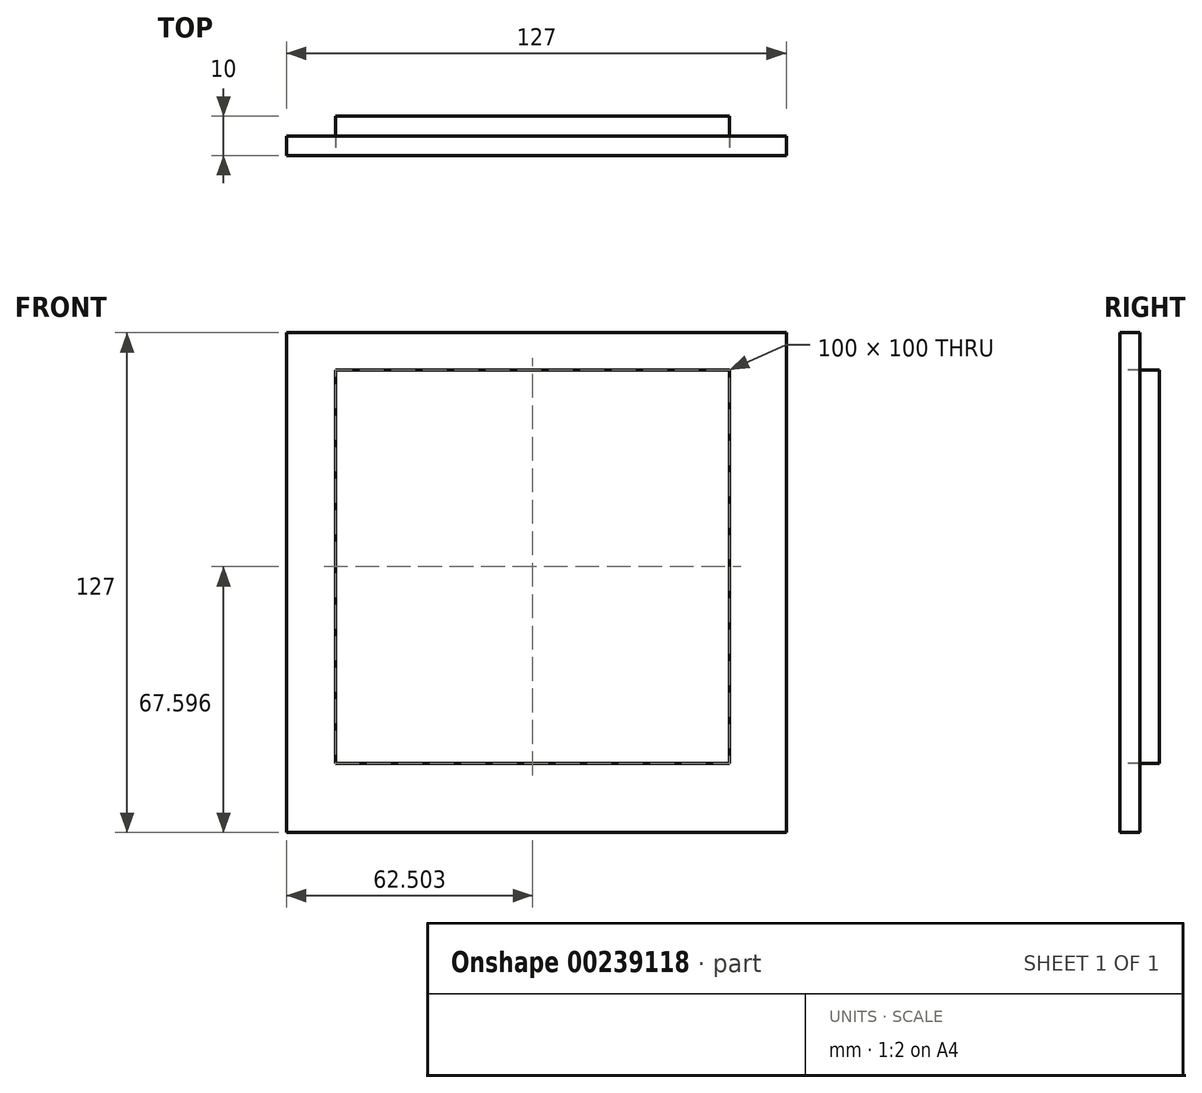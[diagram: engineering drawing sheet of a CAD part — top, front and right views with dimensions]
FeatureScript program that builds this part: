
annotation { "Feature Type Name" : "Feature", "Feature Type Description" : "" }
export const myFeature = defineFeature(function(context is Context, id is Id, definition is map)
    precondition{}
    {
        {
            assignVariable(context, id + "F0", {"name" : "L", "anyValue" : 5});
        }
        {
            var Q0;
            Q0=qCreatedBy(makeId("Front.planeOp"),FACE);
            var sketch = newSketch(context, id + "F1", { "sketchPlane" : qUnion([Q0])});
            skLineSegment(sketch, "E0.bottom", {"start": v(63.5, 63.5) * mm, "end": v(-63.5, 63.5) * mm});
            skLineSegment(sketch, "E0.top", {"start": v(63.5, -63.5) * mm, "end": v(-63.5, -63.5) * mm});
            skLineSegment(sketch, "E0.left", {"start": v(63.5, 63.5) * mm, "end": v(63.5, -63.5) * mm});
            skLineSegment(sketch, "E0.right", {"start": v(-63.5, 63.5) * mm, "end": v(-63.5, -63.5) * mm});
            skPoint(sketch, "E0.middle", {"position": v(0, 0) * mm});
            skSolve(sketch);
        }
        {
            var Q0;
            Q0 = qSketchRegion(id + "F1", true);
            extrude(context, id + "F2", {"entities" : qUnion([Q0]), "endBound" : BoundingType.SYMMETRIC, "depth" : (getVariable(context, 'L')) * mm});
        }
        {
            var Q0;
            Q0=makeQuery(id+"F2.opExtrude","CAP_FACE",FACE,{"disambiguationData":[OSD([sQuery(id+"F1.wireOp",EDGE,"E0.bottom"),sQuery(id+"F1.wireOp",EDGE,"E0.top"),sQuery(id+"F1.wireOp",EDGE,"E0.left"),sQuery(id+"F1.wireOp",EDGE,"E0.right")])],"isStart":false});
            var sketch = newSketch(context, id + "F3", { "sketchPlane" : qUnion([Q0])});
            skLineSegment(sketch, "E1.bottom", {"start": v(49, -45.9) * mm, "end": v(-51, -45.9) * mm});
            skLineSegment(sketch, "E1.top", {"start": v(49, 54.1) * mm, "end": v(-51, 54.1) * mm});
            skLineSegment(sketch, "E1.left", {"start": v(49, -45.9) * mm, "end": v(49, 54.1) * mm});
            skLineSegment(sketch, "E1.right", {"start": v(-51, -45.9) * mm, "end": v(-51, 54.1) * mm});
            skSolve(sketch);
        }
        {
            var Q0;
            Q0 = qSketchRegion(id + "F3", true);
            extrude(context, id + "F4", {"entities" : qUnion([Q0]), "operationType" : NewBodyOperationType.REMOVE, "oppositeDirection" : true, "depth" : 25 * mm});
        }
        {
            var Q0;
            Q0 = qSketchRegion(id + "F3", true);
            extrude(context, id + "F5", {"entities" : qUnion([Q0]), "operationType" : NewBodyOperationType.REMOVE, "oppositeDirection" : true, "depth" : (getVariable(context, 'L')) * mm});
        }
        {
            var Q0;
            Q0=makeQuery(id+"F2.opExtrude","CAP_FACE",FACE,{"disambiguationData":[OSD([sQuery(id+"F1.wireOp",EDGE,"E0.bottom"),sQuery(id+"F1.wireOp",EDGE,"E0.top"),sQuery(id+"F1.wireOp",EDGE,"E0.left"),sQuery(id+"F1.wireOp",EDGE,"E0.right")])],"isStart":true});
            var sketch = newSketch(context, id + "F6", { "sketchPlane" : qUnion([Q0])});
            skLineSegment(sketch, "E2.0", {"start": v(-49, -45.9) * mm, "end": v(-49, 54.1) * mm});
            skLineSegment(sketch, "E3.0", {"start": v(-49, -45.9) * mm, "end": v(51, -45.9) * mm});
            skLineSegment(sketch, "E4.0", {"start": v(51, -45.9) * mm, "end": v(51, 54.1) * mm});
            skLineSegment(sketch, "E5.0", {"start": v(-49, 54.1) * mm, "end": v(51, 54.1) * mm});
            skSolve(sketch);
        }
        {
            var Q0;
            Q0 = qSketchRegion(id + "F6", true);
            extrude(context, id + "F7", {"entities" : qUnion([Q0]), "operationType" : NewBodyOperationType.ADD, "depth" : (getVariable(context, 'L')) * mm});
        }
    });
